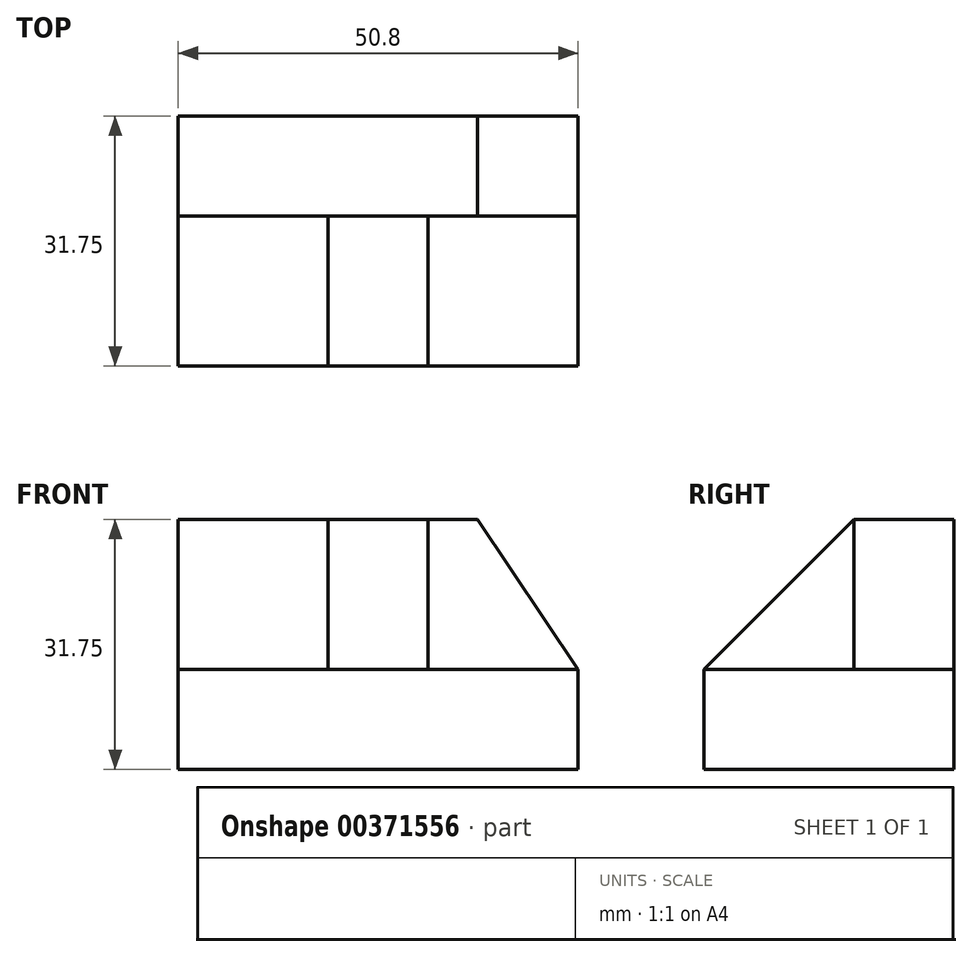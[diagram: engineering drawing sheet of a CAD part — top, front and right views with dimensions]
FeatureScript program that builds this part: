
annotation { "Feature Type Name" : "Feature", "Feature Type Description" : "" }
export const myFeature = defineFeature(function(context is Context, id is Id, definition is map)
    precondition{}
    {
        {
            var Q0;
            Q0=qCreatedBy(makeId("Front.planeOp"),FACE);
            var sketch = newSketch(context, id + "F0", { "sketchPlane" : qUnion([Q0])});
            skLineSegment(sketch, "E0", {"start": v(0, 0) * mm, "end": v(50.8, 0) * mm});
            skLineSegment(sketch, "E1", {"start": v(50.8, 0) * mm, "end": v(50.8, 12.7) * mm});
            skLineSegment(sketch, "E2", {"start": v(50.8, 12.7) * mm, "end": v(38.04, 31.75) * mm});
            skLineSegment(sketch, "E3", {"start": v(38.04, 31.75) * mm, "end": v(0, 31.75) * mm});
            skLineSegment(sketch, "E4", {"start": v(0, 31.75) * mm, "end": v(0, 0) * mm});
            skSolve(sketch);
        }
        {
            var Q0;
            Q0 = qSketchRegion(id + "F0", true);
            extrude(context, id + "F1", {"entities" : qUnion([Q0]), "depth" : 31.75 * mm});
        }
        {
            var Q0;
            Q0=makeQuery(id+"F1.opExtrude","CAP_FACE",FACE,{"disambiguationData":[OSD([sQuery(id+"F0.wireOp",EDGE,"E0"),sQuery(id+"F0.wireOp",EDGE,"E1"),sQuery(id+"F0.wireOp",EDGE,"E2"),sQuery(id+"F0.wireOp",EDGE,"E3"),sQuery(id+"F0.wireOp",EDGE,"E4")])],"isStart":false});
            var sketch = newSketch(context, id + "F2", { "sketchPlane" : qUnion([Q0])});
            skLineSegment(sketch, "E5", {"start": v(0, 12.7) * mm, "end": v(19.05, 12.7) * mm});
            skLineSegment(sketch, "E6", {"start": v(19.05, 12.7) * mm, "end": v(19.05, 31.75) * mm});
            skSolve(sketch);
        }
        {
            var Q0;
            Q0 = qSketchRegion(id + "F2", true);
            var Q1;
            {var subQ0=sQuery(id+"F2.wireOp",EDGE,"E5");Q1=makeQuery(id+"F2.imprint","IMPRINT",FACE,{"disambiguationData":[TD([[makeQuery(id+"F2.imprint","IMPRINT",EDGE,{"derivedFrom":subQ0}),1.0]])]});}
            extrude(context, id + "F3", {"entities" : qUnion([Q0, Q1]), "operationType" : NewBodyOperationType.REMOVE, "oppositeDirection" : true, "depth" : 19.05 * mm});
        }
        {
            var Q0;
            Q0=makeQuery(id+"F1.opExtrude","CAP_FACE",FACE,{"disambiguationData":[OSD([sQuery(id+"F0.wireOp",EDGE,"E0"),sQuery(id+"F0.wireOp",EDGE,"E1"),sQuery(id+"F0.wireOp",EDGE,"E2"),sQuery(id+"F0.wireOp",EDGE,"E3"),sQuery(id+"F0.wireOp",EDGE,"E4")])],"isStart":false});
            var sketch = newSketch(context, id + "F4", { "sketchPlane" : qUnion([Q0])});
            skLineSegment(sketch, "E7", {"start": v(50.8, 12.7) * mm, "end": v(31.75, 12.7) * mm});
            skLineSegment(sketch, "E8", {"start": v(31.75, 12.7) * mm, "end": v(31.75, 31.75) * mm});
            skSolve(sketch);
        }
        {
            var Q0;
            Q0 = qSketchRegion(id + "F4", true);
            var Q1;
            Q1=makeQuery(id+"F4.imprint","IMPRINT",FACE,{"disambiguationData":[TD([[makeQuery(id+"F4.imprint","IMPRINT",EDGE,{"derivedFrom":sQuery(id+"F4.wireOp",EDGE,"E7")}),-1.0]])]});
            extrude(context, id + "F5", {"entities" : qUnion([Q0, Q1]), "operationType" : NewBodyOperationType.REMOVE, "oppositeDirection" : true, "depth" : 19.05 * mm});
        }
        {
            var Q0;
            Q0=makeQuery(id+"F5.boolean.opBoolean","COPY",FACE,{"derivedFrom":makeQuery(id+"F5.opExtrude","SWEPT_FACE",FACE,{"disambiguationData":[OSD([sQuery(id+"F4.wireOp",EDGE,"E8")])]})});
            var sketch = newSketch(context, id + "F6", { "sketchPlane" : qUnion([Q0])});
            skLineSegment(sketch, "E9", {"start": v(-12.7, 31.75) * mm, "end": v(-31.75, 12.7) * mm});
            skSolve(sketch);
        }
        {
            var Q0;
            Q0 = qSketchRegion(id + "F6", true);
            var Q1;
            Q1=makeQuery(id+"F6.imprint","IMPRINT",FACE,{"disambiguationData":[TD([[makeQuery(id+"F6.imprint","IMPRINT",EDGE,{"derivedFrom":sQuery(id+"F6.wireOp",EDGE,"E9")}),-1.0]])]});
            extrude(context, id + "F7", {"entities" : qUnion([Q0, Q1]), "operationType" : NewBodyOperationType.REMOVE, "oppositeDirection" : true, "depth" : 25.4 * mm});
        }
    });
